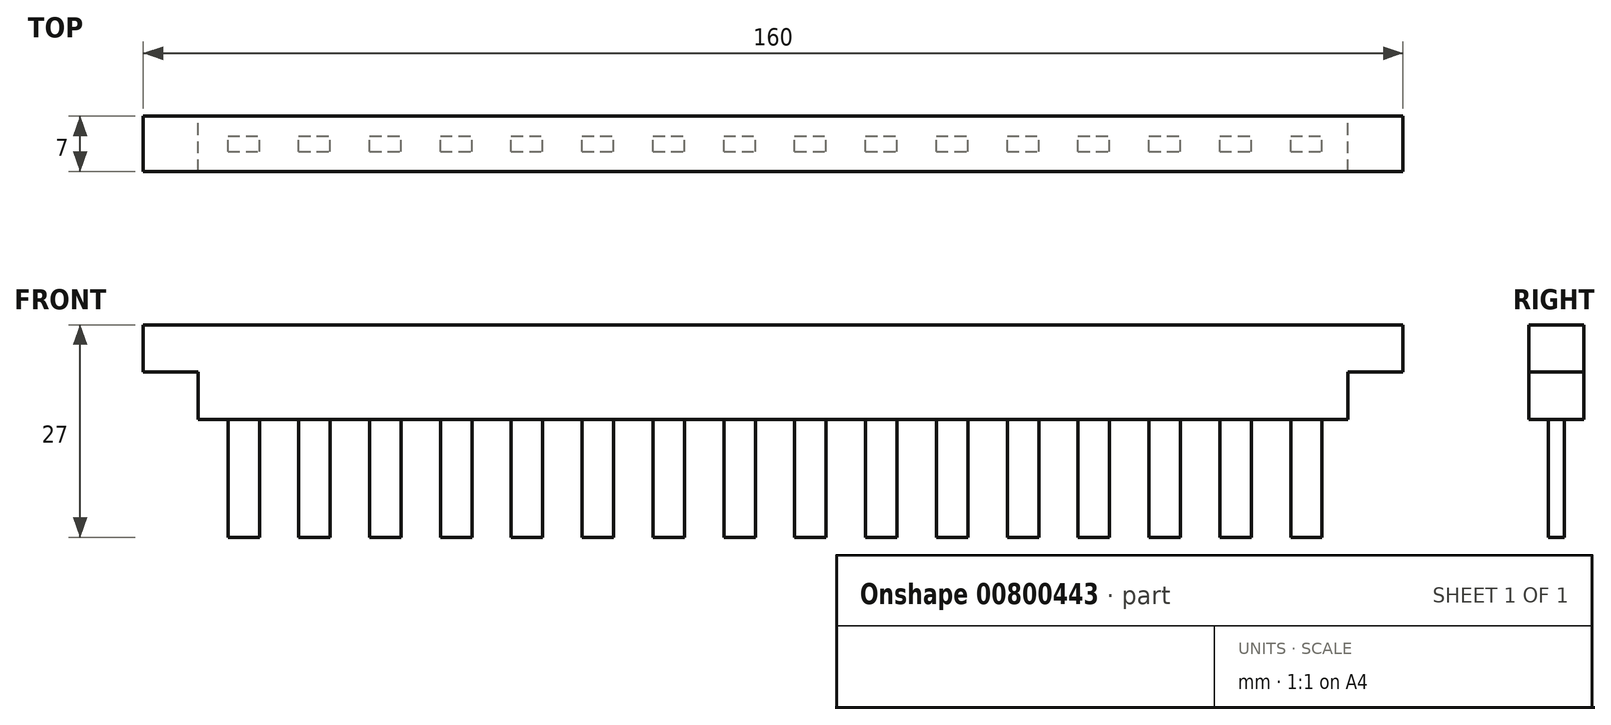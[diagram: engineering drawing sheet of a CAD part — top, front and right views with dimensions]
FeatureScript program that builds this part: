
annotation { "Feature Type Name" : "Feature", "Feature Type Description" : "" }
export const myFeature = defineFeature(function(context is Context, id is Id, definition is map)
    precondition{}
    {
        {
            var Q0;
            Q0=qCreatedBy(makeId("Front.planeOp"),FACE);
            var sketch = newSketch(context, id + "F0", { "sketchPlane" : qUnion([Q0])});
            skLineSegment(sketch, "E0.bottom", {"start": v(80, 3) * mm, "end": v(-80, 3) * mm});
            skLineSegment(sketch, "E0.top", {"start": v(80, -3) * mm, "end": v(-80, -3) * mm});
            skLineSegment(sketch, "E0.left", {"start": v(80, 3) * mm, "end": v(80, -3) * mm});
            skLineSegment(sketch, "E0.right", {"start": v(-80, 3) * mm, "end": v(-80, -3) * mm});
            skPoint(sketch, "E0.middle", {"position": v(0, 0) * mm});
            skPoint(sketch, "E1.middle", {"position": v(80, 3) * mm});
            skPoint(sketch, "E2.middle", {"position": v(0, 3) * mm});
            skLineSegment(sketch, "E3.bottom", {"start": v(-73, -3) * mm, "end": v(73, -3) * mm});
            skLineSegment(sketch, "E3.top", {"start": v(-73, -9) * mm, "end": v(73, -9) * mm});
            skLineSegment(sketch, "E3.left", {"start": v(-73, -3) * mm, "end": v(-73, -9) * mm});
            skLineSegment(sketch, "E3.right", {"start": v(73, -3) * mm, "end": v(73, -9) * mm});
            skLineSegment(sketch, "E4.bottom", {"start": v(-69.25, -9) * mm, "end": v(-65.25, -9) * mm});
            skLineSegment(sketch, "E4.top", {"start": v(-69.25, -24) * mm, "end": v(-65.25, -24) * mm});
            skLineSegment(sketch, "E4.left", {"start": v(-69.25, -9) * mm, "end": v(-69.25, -24) * mm});
            skLineSegment(sketch, "E4.right", {"start": v(-65.25, -9) * mm, "end": v(-65.25, -24) * mm});
            skLineSegment(sketch, "E5.1.0.0", {"start": v(-60.25, -24) * mm, "end": v(-56.25, -24) * mm});
            skLineSegment(sketch, "E5.1.0.1", {"start": v(-60.25, -9) * mm, "end": v(-56.25, -9) * mm});
            skLineSegment(sketch, "E5.1.0.2", {"start": v(-60.25, -9) * mm, "end": v(-60.25, -24) * mm});
            skLineSegment(sketch, "E5.1.0.3", {"start": v(-56.25, -9) * mm, "end": v(-56.25, -24) * mm});
            skLineSegment(sketch, "E5.2.0.0", {"start": v(-51.25, -24) * mm, "end": v(-47.25, -24) * mm});
            skLineSegment(sketch, "E5.2.0.1", {"start": v(-51.25, -9) * mm, "end": v(-47.25, -9) * mm});
            skLineSegment(sketch, "E5.2.0.2", {"start": v(-51.25, -9) * mm, "end": v(-51.25, -24) * mm});
            skLineSegment(sketch, "E5.2.0.3", {"start": v(-47.25, -9) * mm, "end": v(-47.25, -24) * mm});
            skLineSegment(sketch, "E5.3.0.0", {"start": v(-42.25, -24) * mm, "end": v(-38.25, -24) * mm});
            skLineSegment(sketch, "E5.3.0.1", {"start": v(-42.25, -9) * mm, "end": v(-38.25, -9) * mm});
            skLineSegment(sketch, "E5.3.0.2", {"start": v(-42.25, -9) * mm, "end": v(-42.25, -24) * mm});
            skLineSegment(sketch, "E5.3.0.3", {"start": v(-38.25, -9) * mm, "end": v(-38.25, -24) * mm});
            skLineSegment(sketch, "E5.4.0.0", {"start": v(-33.25, -24) * mm, "end": v(-29.25, -24) * mm});
            skLineSegment(sketch, "E5.4.0.1", {"start": v(-33.25, -9) * mm, "end": v(-29.25, -9) * mm});
            skLineSegment(sketch, "E5.4.0.2", {"start": v(-33.25, -9) * mm, "end": v(-33.25, -24) * mm});
            skLineSegment(sketch, "E5.4.0.3", {"start": v(-29.25, -9) * mm, "end": v(-29.25, -24) * mm});
            skLineSegment(sketch, "E5.5.0.0", {"start": v(-24.25, -24) * mm, "end": v(-20.25, -24) * mm});
            skLineSegment(sketch, "E5.5.0.1", {"start": v(-24.25, -9) * mm, "end": v(-20.25, -9) * mm});
            skLineSegment(sketch, "E5.5.0.2", {"start": v(-24.25, -9) * mm, "end": v(-24.25, -24) * mm});
            skLineSegment(sketch, "E5.5.0.3", {"start": v(-20.25, -9) * mm, "end": v(-20.25, -24) * mm});
            skLineSegment(sketch, "E5.6.0.0", {"start": v(-15.25, -24) * mm, "end": v(-11.25, -24) * mm});
            skLineSegment(sketch, "E5.6.0.1", {"start": v(-15.25, -9) * mm, "end": v(-11.25, -9) * mm});
            skLineSegment(sketch, "E5.6.0.2", {"start": v(-15.25, -9) * mm, "end": v(-15.25, -24) * mm});
            skLineSegment(sketch, "E5.6.0.3", {"start": v(-11.25, -9) * mm, "end": v(-11.25, -24) * mm});
            skLineSegment(sketch, "E5.7.0.0", {"start": v(-6.25, -24) * mm, "end": v(-2.25, -24) * mm});
            skLineSegment(sketch, "E5.7.0.1", {"start": v(-6.25, -9) * mm, "end": v(-2.25, -9) * mm});
            skLineSegment(sketch, "E5.7.0.2", {"start": v(-6.25, -9) * mm, "end": v(-6.25, -24) * mm});
            skLineSegment(sketch, "E5.7.0.3", {"start": v(-2.25, -9) * mm, "end": v(-2.25, -24) * mm});
            skLineSegment(sketch, "E5.8.0.0", {"start": v(2.75, -24) * mm, "end": v(6.75, -24) * mm});
            skLineSegment(sketch, "E5.8.0.1", {"start": v(2.75, -9) * mm, "end": v(6.75, -9) * mm});
            skLineSegment(sketch, "E5.8.0.2", {"start": v(2.75, -9) * mm, "end": v(2.75, -24) * mm});
            skLineSegment(sketch, "E5.8.0.3", {"start": v(6.75, -9) * mm, "end": v(6.75, -24) * mm});
            skLineSegment(sketch, "E5.9.0.0", {"start": v(11.75, -24) * mm, "end": v(15.75, -24) * mm});
            skLineSegment(sketch, "E5.9.0.1", {"start": v(11.75, -9) * mm, "end": v(15.75, -9) * mm});
            skLineSegment(sketch, "E5.9.0.2", {"start": v(11.75, -9) * mm, "end": v(11.75, -24) * mm});
            skLineSegment(sketch, "E5.9.0.3", {"start": v(15.75, -9) * mm, "end": v(15.75, -24) * mm});
            skLineSegment(sketch, "E5.10.0.0", {"start": v(20.75, -24) * mm, "end": v(24.75, -24) * mm});
            skLineSegment(sketch, "E5.10.0.1", {"start": v(20.75, -9) * mm, "end": v(24.75, -9) * mm});
            skLineSegment(sketch, "E5.10.0.2", {"start": v(20.75, -9) * mm, "end": v(20.75, -24) * mm});
            skLineSegment(sketch, "E5.10.0.3", {"start": v(24.75, -9) * mm, "end": v(24.75, -24) * mm});
            skLineSegment(sketch, "E5.11.0.0", {"start": v(29.75, -24) * mm, "end": v(33.75, -24) * mm});
            skLineSegment(sketch, "E5.11.0.1", {"start": v(29.75, -9) * mm, "end": v(33.75, -9) * mm});
            skLineSegment(sketch, "E5.11.0.2", {"start": v(29.75, -9) * mm, "end": v(29.75, -24) * mm});
            skLineSegment(sketch, "E5.11.0.3", {"start": v(33.75, -9) * mm, "end": v(33.75, -24) * mm});
            skLineSegment(sketch, "E5.12.0.0", {"start": v(38.75, -24) * mm, "end": v(42.75, -24) * mm});
            skLineSegment(sketch, "E5.12.0.1", {"start": v(38.75, -9) * mm, "end": v(42.75, -9) * mm});
            skLineSegment(sketch, "E5.12.0.2", {"start": v(38.75, -9) * mm, "end": v(38.75, -24) * mm});
            skLineSegment(sketch, "E5.12.0.3", {"start": v(42.75, -9) * mm, "end": v(42.75, -24) * mm});
            skLineSegment(sketch, "E5.13.0.0", {"start": v(47.75, -24) * mm, "end": v(51.75, -24) * mm});
            skLineSegment(sketch, "E5.13.0.1", {"start": v(47.75, -9) * mm, "end": v(51.75, -9) * mm});
            skLineSegment(sketch, "E5.13.0.2", {"start": v(47.75, -9) * mm, "end": v(47.75, -24) * mm});
            skLineSegment(sketch, "E5.13.0.3", {"start": v(51.75, -9) * mm, "end": v(51.75, -24) * mm});
            skLineSegment(sketch, "E5.14.0.0", {"start": v(56.75, -24) * mm, "end": v(60.75, -24) * mm});
            skLineSegment(sketch, "E5.14.0.1", {"start": v(56.75, -9) * mm, "end": v(60.75, -9) * mm});
            skLineSegment(sketch, "E5.14.0.2", {"start": v(56.75, -9) * mm, "end": v(56.75, -24) * mm});
            skLineSegment(sketch, "E5.14.0.3", {"start": v(60.75, -9) * mm, "end": v(60.75, -24) * mm});
            skLineSegment(sketch, "E5.15.0.0", {"start": v(65.75, -24) * mm, "end": v(69.75, -24) * mm});
            skLineSegment(sketch, "E5.15.0.1", {"start": v(65.75, -9) * mm, "end": v(69.75, -9) * mm});
            skLineSegment(sketch, "E5.15.0.2", {"start": v(65.75, -9) * mm, "end": v(65.75, -24) * mm});
            skLineSegment(sketch, "E5.15.0.3", {"start": v(69.75, -9) * mm, "end": v(69.75, -24) * mm});
            skSolve(sketch);
        }
        {
            var Q0;
            Q0=makeQuery(id+"F0.imprint","IMPRINT",FACE,{"disambiguationData":[TD([[makeQuery(id+"F0.imprint","IMPRINT",EDGE,{"derivedFrom":sQuery(id+"F0.wireOp",EDGE,"E0.bottom")}),1.0]])]});
            var Q1;
            {var subQ25=sQuery(id+"F0.wireOp",EDGE,"E3.left");Q1=makeQuery(id+"F0.imprint","IMPRINT",FACE,{"disambiguationData":[TD([[makeQuery(id+"F0.imprint","IMPRINT",EDGE,{"derivedFrom":subQ25}),1.0]])]});}
            extrude(context, id + "F1", {"entities" : qUnion([Q0, Q1]), "depth" : 7 * mm, "offsetDistance" : 25.4 * mm, "symmetric" : true});
        }
        {
            var Q0;
            Q0=makeQuery(id+"F0.imprint","IMPRINT",FACE,{"disambiguationData":[TD([[makeQuery(id+"F0.imprint","IMPRINT",EDGE,{"derivedFrom":sQuery(id+"F0.wireOp",EDGE,"E5.15.0.0")}),1.0]])]});
            var Q1;
            Q1=makeQuery(id+"F0.imprint","IMPRINT",FACE,{"disambiguationData":[TD([[makeQuery(id+"F0.imprint","IMPRINT",EDGE,{"derivedFrom":sQuery(id+"F0.wireOp",EDGE,"E5.14.0.0")}),1.0]])]});
            var Q2;
            Q2=makeQuery(id+"F0.imprint","IMPRINT",FACE,{"disambiguationData":[TD([[makeQuery(id+"F0.imprint","IMPRINT",EDGE,{"derivedFrom":sQuery(id+"F0.wireOp",EDGE,"E5.13.0.0")}),1.0]])]});
            var Q3;
            Q3=makeQuery(id+"F0.imprint","IMPRINT",FACE,{"disambiguationData":[TD([[makeQuery(id+"F0.imprint","IMPRINT",EDGE,{"derivedFrom":sQuery(id+"F0.wireOp",EDGE,"E5.12.0.0")}),1.0]])]});
            var Q4;
            Q4=makeQuery(id+"F0.imprint","IMPRINT",FACE,{"disambiguationData":[TD([[makeQuery(id+"F0.imprint","IMPRINT",EDGE,{"derivedFrom":sQuery(id+"F0.wireOp",EDGE,"E5.11.0.0")}),1.0]])]});
            var Q5;
            Q5=makeQuery(id+"F0.imprint","IMPRINT",FACE,{"disambiguationData":[TD([[makeQuery(id+"F0.imprint","IMPRINT",EDGE,{"derivedFrom":sQuery(id+"F0.wireOp",EDGE,"E5.10.0.0")}),1.0]])]});
            var Q6;
            Q6=makeQuery(id+"F0.imprint","IMPRINT",FACE,{"disambiguationData":[TD([[makeQuery(id+"F0.imprint","IMPRINT",EDGE,{"derivedFrom":sQuery(id+"F0.wireOp",EDGE,"E5.9.0.0")}),1.0]])]});
            var Q7;
            Q7=makeQuery(id+"F0.imprint","IMPRINT",FACE,{"disambiguationData":[TD([[makeQuery(id+"F0.imprint","IMPRINT",EDGE,{"derivedFrom":sQuery(id+"F0.wireOp",EDGE,"E5.8.0.0")}),1.0]])]});
            var Q8;
            Q8=makeQuery(id+"F0.imprint","IMPRINT",FACE,{"disambiguationData":[TD([[makeQuery(id+"F0.imprint","IMPRINT",EDGE,{"derivedFrom":sQuery(id+"F0.wireOp",EDGE,"E5.7.0.0")}),1.0]])]});
            var Q9;
            Q9=makeQuery(id+"F0.imprint","IMPRINT",FACE,{"disambiguationData":[TD([[makeQuery(id+"F0.imprint","IMPRINT",EDGE,{"derivedFrom":sQuery(id+"F0.wireOp",EDGE,"E5.6.0.0")}),1.0]])]});
            var Q10;
            Q10=makeQuery(id+"F0.imprint","IMPRINT",FACE,{"disambiguationData":[TD([[makeQuery(id+"F0.imprint","IMPRINT",EDGE,{"derivedFrom":sQuery(id+"F0.wireOp",EDGE,"E5.5.0.0")}),1.0]])]});
            var Q11;
            Q11=makeQuery(id+"F0.imprint","IMPRINT",FACE,{"disambiguationData":[TD([[makeQuery(id+"F0.imprint","IMPRINT",EDGE,{"derivedFrom":sQuery(id+"F0.wireOp",EDGE,"E5.4.0.0")}),1.0]])]});
            var Q12;
            Q12=makeQuery(id+"F0.imprint","IMPRINT",FACE,{"disambiguationData":[TD([[makeQuery(id+"F0.imprint","IMPRINT",EDGE,{"derivedFrom":sQuery(id+"F0.wireOp",EDGE,"E5.3.0.0")}),1.0]])]});
            var Q13;
            Q13=makeQuery(id+"F0.imprint","IMPRINT",FACE,{"disambiguationData":[TD([[makeQuery(id+"F0.imprint","IMPRINT",EDGE,{"derivedFrom":sQuery(id+"F0.wireOp",EDGE,"E5.2.0.0")}),1.0]])]});
            var Q14;
            Q14=makeQuery(id+"F0.imprint","IMPRINT",FACE,{"disambiguationData":[TD([[makeQuery(id+"F0.imprint","IMPRINT",EDGE,{"derivedFrom":sQuery(id+"F0.wireOp",EDGE,"E5.1.0.0")}),1.0]])]});
            var Q15;
            Q15=makeQuery(id+"F0.imprint","IMPRINT",FACE,{"disambiguationData":[TD([[makeQuery(id+"F0.imprint","IMPRINT",EDGE,{"derivedFrom":sQuery(id+"F0.wireOp",EDGE,"E4.top")}),1.0]])]});
            extrude(context, id + "F2", {"entities" : qUnion([Q0, Q1, Q2, Q3, Q4, Q5, Q6, Q7, Q8, Q9, Q10, Q11, Q12, Q13, Q14, Q15]), "operationType" : NewBodyOperationType.ADD, "depth" : 2 * mm, "offsetDistance" : 25.4 * mm, "symmetric" : true});
        }
    });
